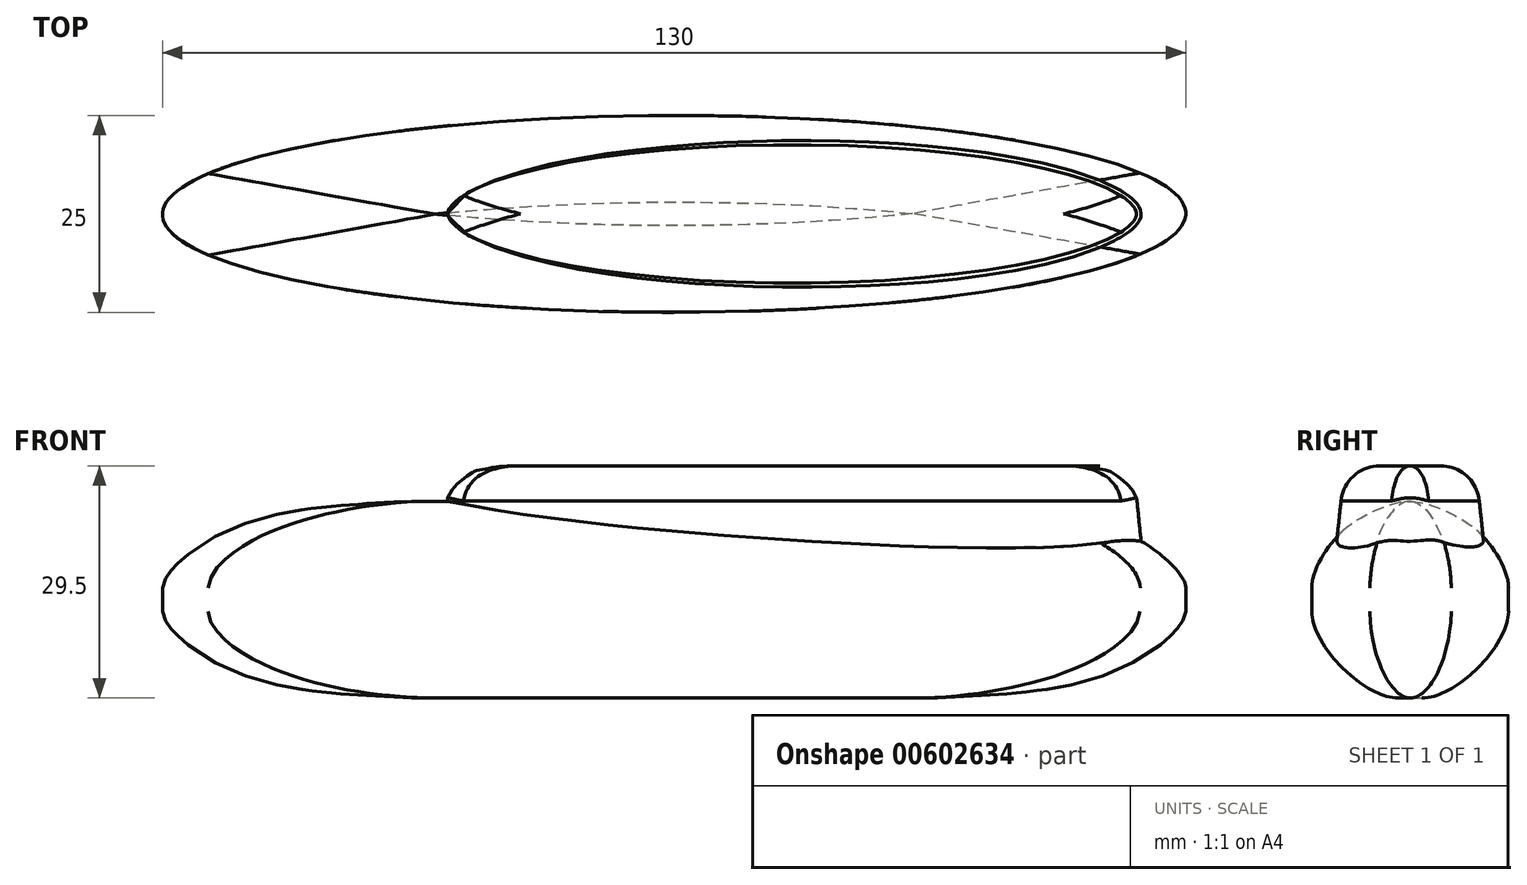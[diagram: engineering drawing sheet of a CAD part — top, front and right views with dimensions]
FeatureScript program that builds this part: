
annotation { "Feature Type Name" : "Feature", "Feature Type Description" : "" }
export const myFeature = defineFeature(function(context is Context, id is Id, definition is map)
    precondition{}
    {
        {
            var Q0;
            Q0=qCreatedBy(makeId("Top.planeOp"),FACE);
            var sketch = newSketch(context, id + "F0", { "sketchPlane" : qUnion([Q0])});
            skEllipse(sketch, "E0", {"center": v(0, 0) * mm, "majorRadius": 65 * mm, "minorRadius": 12.5 * mm, "majorAxis": v(1, 0)});
            skSolve(sketch);
        }
        {
            var Q0;
            Q0=makeQuery(id+"F0.imprint","IMPRINT",FACE,{"disambiguationData":[TD([[makeQuery(id+"F0.imprint","IMPRINT",EDGE,{"derivedFrom":sQuery(id+"F0.wireOp",EDGE,"E0")}),1.0]])]});
            extrude(context, id + "F1", {"entities" : qUnion([Q0]), "endBound" : BoundingType.SYMMETRIC, "depth" : 25 * mm, "offsetDistance" : 25 * mm});
        }
        {
            var Q0;
            Q0=makeQuery(id+"F1.opExtrude","CAP_FACE",FACE,{"disambiguationData":[OSD([sQuery(id+"F0.wireOp",EDGE,"E0")])],"isStart":true});
            var Q1;
            Q1=makeQuery(id+"F1.opExtrude","CAP_EDGE",EDGE,{"disambiguationData":[OSD([sQuery(id+"F0.wireOp",EDGE,"E0")])],"isStart":false});
            fillet(context, id + "F2", {"entities" : qUnion([Q0, Q1]), "radius" : 11 * mm, "tangentPropagation" : true, "rho" : .3, "crossSection" : FilletCrossSection.CONIC, "allowEdgeOverflow" : false});
        }
        {
            var Q0;
            Q0=qCreatedBy(makeId("Top.planeOp"),FACE);
            cPlane(context, id + "F3", {"entities" : qUnion([Q0]), "cplaneType" : CPlaneType.OFFSET, "offset" : 1 * mm, "width" : 150 * mm, "height" : 150 * mm});
        }
        {
            var Q0;
            Q0=qCreatedBy(id+"F3.planeOp",FACE);
            var sketch = newSketch(context, id + "F4", { "sketchPlane" : qUnion([Q0])});
            skEllipse(sketch, "E1", {"center": v(15, 0) * mm, "majorRadius": 45 * mm, "minorRadius": 10 * mm, "majorAxis": v(1, 0)});
            skSolve(sketch);
        }
        {
            var Q0;
            Q0 = qSketchRegion(id + "F4", true);
            extrude(context, id + "F5", {"entities" : qUnion([Q0]), "operationType" : NewBodyOperationType.ADD, "depth" : 16 * mm, "offsetDistance" : 25 * mm, "hasDraft" : true, "draftAngle" : 6 * degree, "draftPullDirection" : true});
        }
        {
            var Q0;
            Q0=makeQuery(id+"F5.opExtrude","CAP_FACE",FACE,{"disambiguationData":[OSD([sQuery(id+"F4.wireOp",EDGE,"E1")])],"isStart":false});
            fillet(context, id + "F6", {"entities" : qUnion([Q0]), "radius" : 5 * mm, "tangentPropagation" : true, "allowEdgeOverflow" : false});
        }
    });
